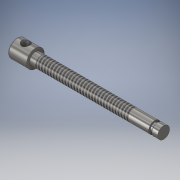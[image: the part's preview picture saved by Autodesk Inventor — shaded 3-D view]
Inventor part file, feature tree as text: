
AUTODESK INVENTOR PART (.ipt)
format: ipt  version: 2017 SP1 (Build 210196100, 196)  size: 145,408 bytes
history: native  units: in
note: dims shown in document units (in); Inventor stores cm internally (conversion verified against a paired STEP export)
features: sketch x3, hole x2, revolve x1, thread x1, fillet x1
ambient origin geometry x8: Origin, YZ Plane, XZ Plane, XY Plane, X Axis, Y Axis, Z Axis, Center Point
bodies: Solid1 (feature_tree)
feature tree (8):
  revolve  "Revolution1"  [1 undecoded]
  thread  "Thread1"  [1 undecoded]
  hole  "Hole1"  [1 undecoded]
  hole  "Hole2"  [1 undecoded]
  fillet  "Fillet1"  Radius=0.25in
  sketch  "Sketch1"  dims[d0=0.375in d1=0.8125in d2=6.25in]
  sketch  "Sketch2"  dims[d4=0.25in d7=0.1875in]
  sketch  "Sketch3"  dims[d8=0.1295in d9=90.0deg d10=0.25in d11=3.9375in d12=0.25in d13=3.9375in d14=0.8705in d15=0.3438in d16=0.3438in d17=0.75in d18=0.375in d19=0.25in d20=0.5635in d21=1.0in d22=0.8108in d23=0.4062in d24=0.3438in d26=0.375in d27=0.4062in d28=0.375in d29=0.3438in d30=0.75in d31=0.375in d32=0.25in d33=0.5635in d34=1.0in d35=0.8108in d36=0.0625in]
note: 4 required parameter values undecoded (feature->parameter linkage not recoverable at this tier; creation-order binding heuristic only, values carry confidence <= 0.55)